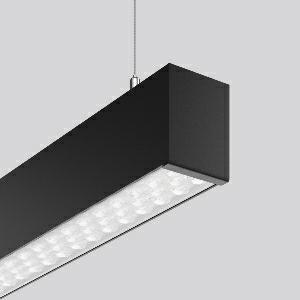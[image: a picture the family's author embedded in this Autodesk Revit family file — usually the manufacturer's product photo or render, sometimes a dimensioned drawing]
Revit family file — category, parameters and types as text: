
# Revit family: linedo_single_ip20_312564_003_76_7236
name_source: partatom
category: Lighting Fixtures
units: mm (PartAtom-declared; Revit-internal decimal feet)

## family parameters
Cut with Voids When Loaded = No
Host = Face
Light Source = No
Part Type = Normal
Room Calculation Point = No
Round Connector Dimension = Use Diameter
Shared = No

## types (1)
- LINEDO single IP20 (1 x LED Modul 830, 6100 lm, 3000)
    Apparent Load = 40 VA
    CIE Flux Codes = 86 96 99 100 100
    Color Rendering = 80
    Color Temperature = 3000
    Default Elevation = 1800 mm
    Description = Series: LINEDO single IP20
Stylish pendant luminaire. Housing: extruded aluminium profile, powder-coated. End cap aluminium powder-coated, without visible screws. High-efficiency LED units with optimum light control thanks to clear plastic (PC) lens optics. 2-point steel cable suspension freely positionable and infinitely height-adjustable. With power cord (2.5 m). Please order canopy separately if required. Perfect for office areas (RUG < 19) and environments with computer screens in accordance with EN 12464-1. 
Colour: deep black, matt (RAL 9005)
Length: 2264 mm
Width: 58 mm
Height: 76 mm
Suspension length: 100-1500 mm
Lamp: LED
Socket: without socket
Colour temperature: 3000K
Colour rendering index (CRI): 80
System power: 40 W
Rated luminous flux: 6100 lm
Beam angle Down: 59°
Luminous efficiency: 153 lm/W
Control gear: Converter, dimmable, DALI
Protection class: I
Type of protection: IP 20
    Height = 76 mm
    Lamp = 1 x LED Modul 830
    Lamp Light Flux = 6100 lm
    Lamp count = 1
    Length = 2264 mm
    Lifetime = 50000 h
    Luminous efficacy = 153 lm/W
    Manufacturer = RZB
    ModVariant = No
    Model = 312564.003.76
    Mounting Place = Ceiling
    Mounting Type = Surface mounted, Pendant
    Number of Poles = 1
    OnlyDefault = Yes
    Power Factor = 1
    Product Name = LINEDO single IP20
    Product group = Pendant luminaires
    ProductGroupID = 902
    Protection Class = Protection class I
    Protection Degree = IP 20
    RLX_Detail_Level = 1
    RLX_Emergency_Light_Flux = 0 lm
    RLX_Emergency_Type = 0
    RLX_Emergency_Type_DB = No
    RlxData = <blob elided: 35001 chars, md5=ee5014a2>
    Socket = socket
    Standby Power = 0 W
    System Light Flux = 6100 lm
    System Power = 40 W
    Type Comments = ALEA SPOT
    Type Image = 312563.003.jpg
    URL = http://relux.com
    VarID = ---
    Voltage = 230 V
    Voltage Range = 220-240 V
    Weight = 0.00 kg
    Width = 58 mm

## geometry (parser evidence)
native form markers: Blend x4, Sweep x10
no freeform markers — native parametric forms only
